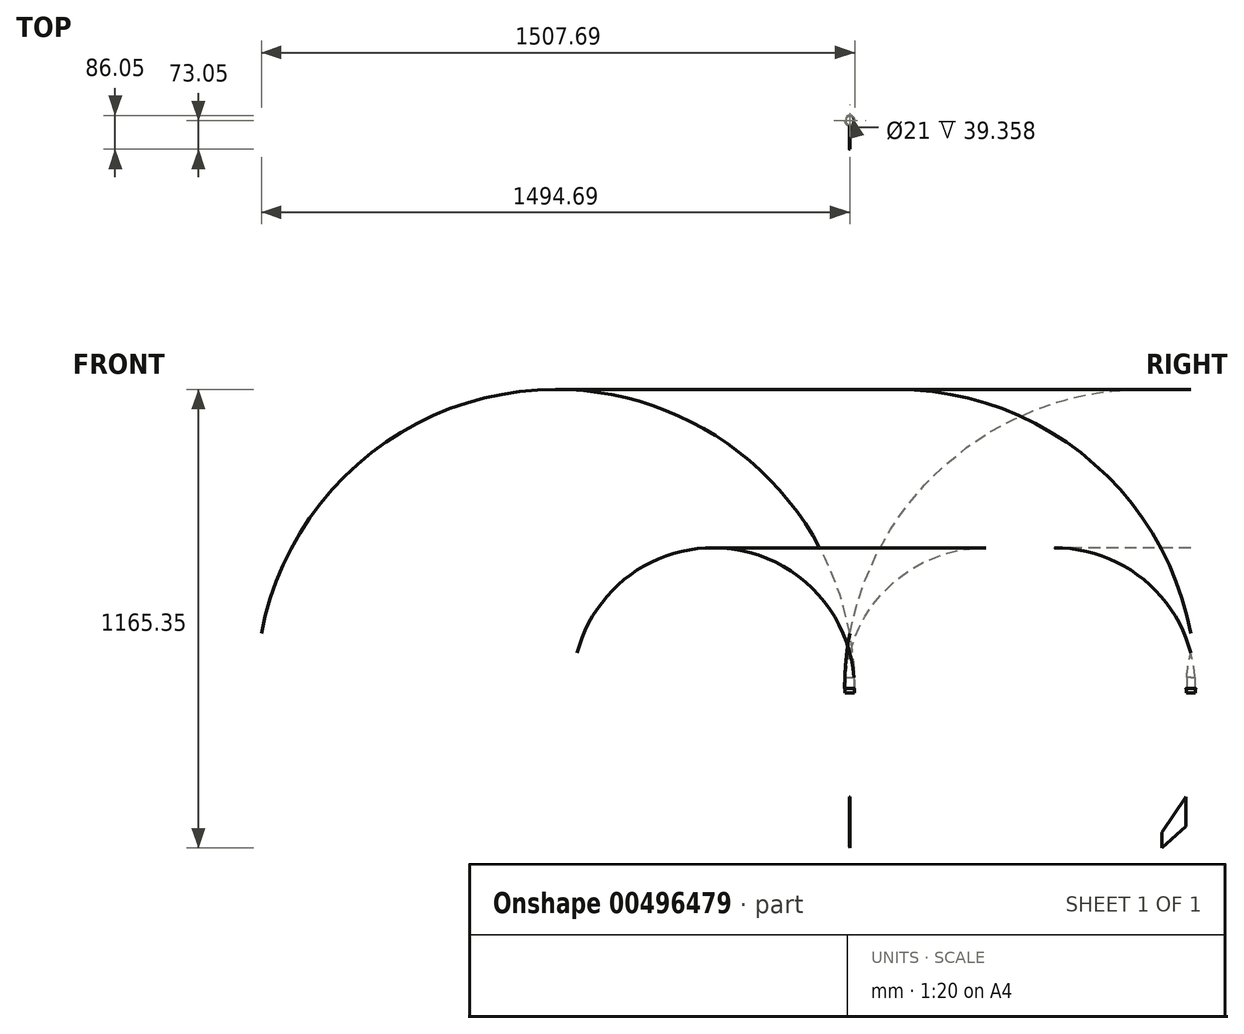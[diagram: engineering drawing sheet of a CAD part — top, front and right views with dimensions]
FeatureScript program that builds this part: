
annotation { "Feature Type Name" : "Feature", "Feature Type Description" : "" }
export const myFeature = defineFeature(function(context is Context, id is Id, definition is map)
    precondition{}
    {
        {
            var Q0;
            Q0=qCreatedBy(makeId("Top.planeOp"),FACE);
            var sketch = newSketch(context, id + "F0", { "sketchPlane" : qUnion([Q0])});
            skCircle(sketch, "E0", {"center": v(0, 0) * mm, "radius": 12 * mm});
            skLineSegment(sketch, "E1", {"start": v(0, 0) * mm, "end": v(12, 0) * mm, "construction": true});
            skCircle(sketch, "E2.0", {"center": v(0, 0) * mm, "radius": 13 * mm});
            skSolve(sketch);
        }
        {
            var Q0;
            Q0=qCreatedBy(makeId("Top.planeOp"),FACE);
            cPlane(context, id + "F1", {"entities" : qUnion([Q0]), "cplaneType" : CPlaneType.OFFSET, "offset" : 350 * mm, "width" : 150 * mm, "height" : 150 * mm});
        }
        {
            var Q0;
            Q0=qCreatedBy(id+"F1.planeOp",FACE);
            var sketch = newSketch(context, id + "F2", { "sketchPlane" : qUnion([Q0])});
            skCircle(sketch, "E3.0", {"center": v(0, 0) * mm, "radius": 11.63 * mm});
            skCircle(sketch, "E4.0", {"center": v(0, 0) * mm, "radius": 13 * mm});
            skCircle(sketch, "E5", {"center": v(0, 0) * mm, "radius": 10.5 * mm});
            skSolve(sketch);
        }
        {
            var Q0;
            Q0=qCreatedBy(makeId("Right.planeOp"),FACE);
            var sketch = newSketch(context, id + "F3", { "sketchPlane" : qUnion([Q0])});
            skLineSegment(sketch, "E6.0", {"start": v(-13, 350) * mm, "end": v(13, 350) * mm});
            skPoint(sketch, "E7.0", {"position": v(0, 350) * mm});
            skLineSegment(sketch, "E8", {"start": v(13, 350) * mm, "end": v(-747.35, 350) * mm, "construction": true});
            skArc(sketch, "E9", {"start": v(13, 350) * mm, "mid": v(9.74, 420.3) * mm, "end": v(0, 490) * mm});
            skLineSegment(sketch, "E10", {"start": v(-13, 350) * mm, "end": v(747.35, 350) * mm, "construction": true});
            skCircle(sketch, "E11", {"center": v(747.35, 350) * mm, "radius": 760.35 * mm, "construction": true});
            skLineSegment(sketch, "E12", {"start": v(0, 350) * mm, "end": v(0, 490) * mm});
            skLineSegment(sketch, "E13.0", {"start": v(-11.63, 350) * mm, "end": v(11.63, 350) * mm});
            skArc(sketch, "E14", {"start": v(11.62, 350) * mm, "mid": v(8.7, 395.61) * mm, "end": v(0, 440.49) * mm});
            skSolve(sketch);
        }
        {
            var Q0;
            {var subQ0=sQuery(id+"F3.wireOp",EDGE,"E9");Q0=makeQuery(id+"F3.imprint","IMPRINT",FACE,{"disambiguationData":[TD([[makeQuery(id+"F3.imprint","IMPRINT",EDGE,{"derivedFrom":subQ0}),1.0]])]});}
            var Q1;
            Q1=sQuery(id+"F3.wireOp",EDGE,"E9");
            var Q2;
            Q2=sQuery(id+"F3.wireOp",EDGE,"E12");
            revolve(context, id + "F4", {"entities" : qUnion([Q0]), "surfaceEntities" : qUnion([Q1]), "axis" : qUnion([Q2]), "revolveType" : RevolveType.FULL});
        }
        {
            var Q0;
            Q0=qCreatedBy(makeId("Right.planeOp"),FACE);
            var sketch = newSketch(context, id + "F5", { "sketchPlane" : qUnion([Q0])});
            skLineSegment(sketch, "E15", {"start": v(-13, 0) * mm, "end": v(-13, 75) * mm});
            skLineSegment(sketch, "E16", {"start": v(-13, 75) * mm, "end": v(-73, -15) * mm});
            skLineSegment(sketch, "E17", {"start": v(-73, -15) * mm, "end": v(-73, -55) * mm});
            skLineSegment(sketch, "E18", {"start": v(-73, -55) * mm, "end": v(-13, 0) * mm});
            skSolve(sketch);
        }
        {
            var Q0;
            Q0=makeQuery(id+"F5.imprint","IMPRINT",FACE,{"disambiguationData":[TD([[makeQuery(id+"F5.imprint","IMPRINT",EDGE,{"derivedFrom":sQuery(id+"F5.wireOp",EDGE,"E15")}),1.0]])]});
            extrude(context, id + "F6", {"entities" : qUnion([Q0]), "endBound" : BoundingType.SYMMETRIC, "depth" : 2 * mm, "hasDraft" : true, "draftAngle" : 3 * degree, "offsetDistance" : 25 * mm});
        }
        {
            var Q0;
            Q0=makeQuery(id+"F6.opExtrude","CAP_EDGE",EDGE,{"disambiguationData":[OSD([sQuery(id+"F5.wireOp",EDGE,"E16")])],"isStart":false});
            var Q1;
            Q1=makeQuery(id+"F6.opExtrude","CAP_EDGE",EDGE,{"disambiguationData":[OSD([sQuery(id+"F5.wireOp",EDGE,"E16")])],"isStart":true});
            fillet(context, id + "F7", {"entities" : qUnion([Q0, Q1]), "radius" : 3 * mm, "tangentPropagation" : true, "allowEdgeOverflow" : false});
        }
        {
            var Q0;
            Q0=makeQuery(id+"F6.opExtrude","CAP_EDGE",EDGE,{"disambiguationData":[OSD([sQuery(id+"F5.wireOp",EDGE,"E18")])],"isStart":false});
            var Q1;
            Q1=makeQuery(id+"F6.opExtrude","CAP_EDGE",EDGE,{"disambiguationData":[OSD([sQuery(id+"F5.wireOp",EDGE,"E18")])],"isStart":true});
            fillet(context, id + "F8", {"entities" : qUnion([Q0, Q1]), "radius" : 320 * mm, "tangentPropagation" : true, "allowEdgeOverflow" : false});
        }
        {
            var Q0;
            Q0=makeQuery(id+"F2.imprint","IMPRINT",FACE,{"disambiguationData":[TD([[makeQuery(id+"F2.imprint","IMPRINT",EDGE,{"derivedFrom":sQuery(id+"F2.wireOp",EDGE,"E3.0")}),1.0]])]});
            var Q1;
            Q1=makeQuery(id+"F4.opRevolve","SWEPT_FACE",FACE,{"disambiguationData":[OSD([sQuery(id+"F3.wireOp",EDGE,"E14")])]});
            extrude(context, id + "F9", {"entities" : qUnion([Q0]), "operationType" : NewBodyOperationType.ADD, "endBound" : BoundingType.UP_TO_SURFACE, "depth" : 40 * mm, "endBoundEntityFace" : qUnion([Q1]), "offsetDistance" : 25 * mm});
        }
        {
            var Q0;
            Q0=makeQuery(id+"F2.imprint","IMPRINT",FACE,{"disambiguationData":[TD([[makeQuery(id+"F2.imprint","IMPRINT",EDGE,{"derivedFrom":sQuery(id+"F2.wireOp",EDGE,"E3.0")}),1.0]])]});
            extrude(context, id + "F10", {"entities" : qUnion([Q0]), "operationType" : NewBodyOperationType.ADD, "oppositeDirection" : true, "depth" : 11 * mm, "offsetDistance" : 25 * mm});
        }
    });
